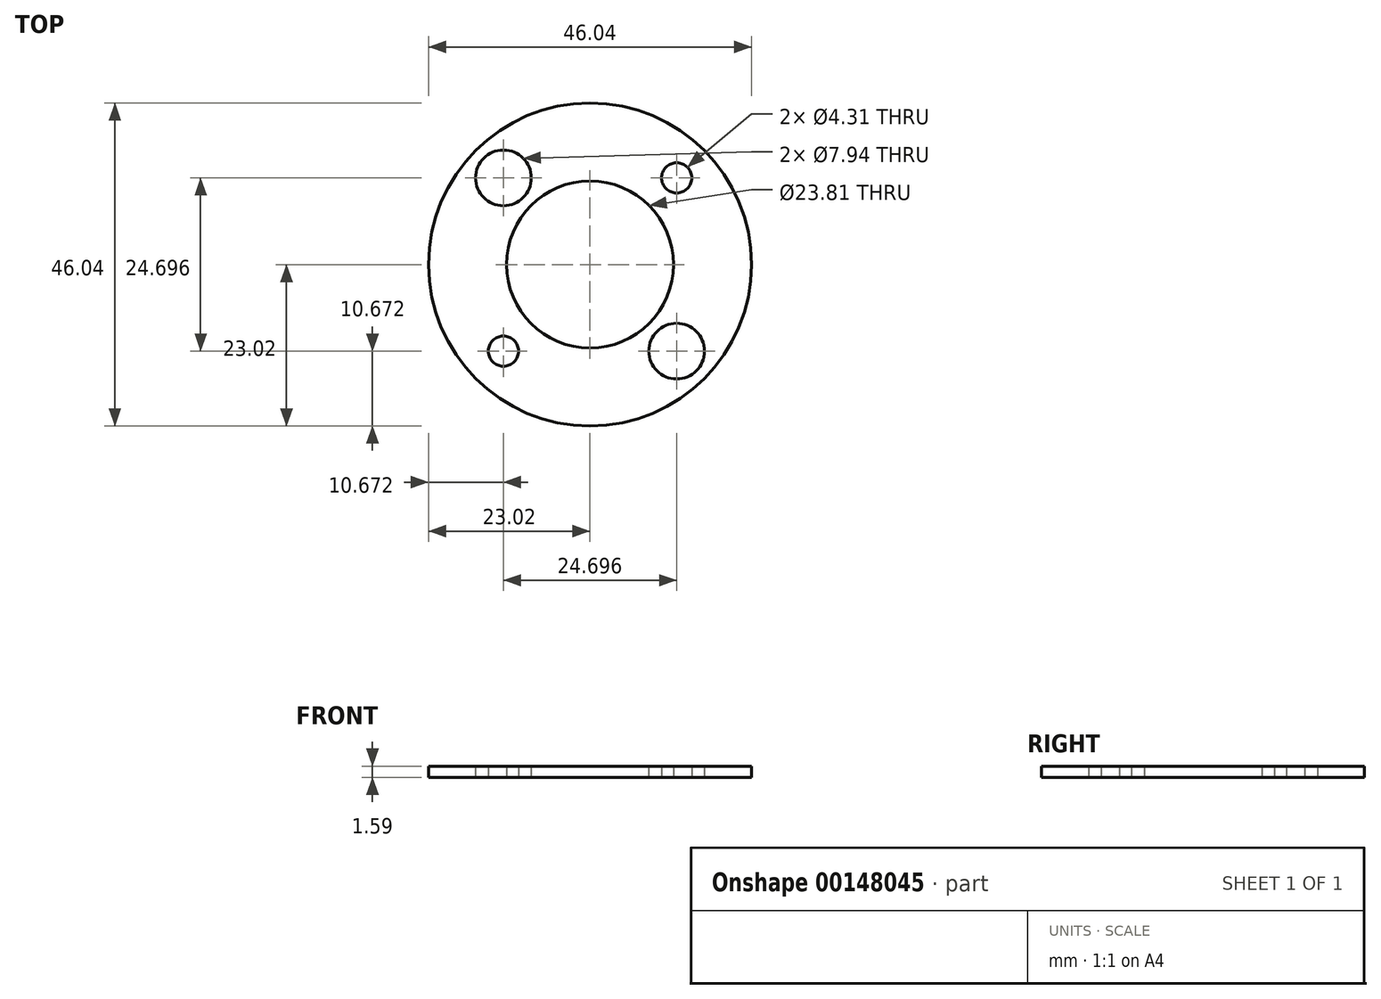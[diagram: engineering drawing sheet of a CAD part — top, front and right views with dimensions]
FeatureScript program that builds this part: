
annotation { "Feature Type Name" : "Feature", "Feature Type Description" : "" }
export const myFeature = defineFeature(function(context is Context, id is Id, definition is map)
    precondition{}
    {
        {
            var Q0;
            Q0=qCreatedBy(makeId("Top.planeOp"),FACE);
            var sketch = newSketch(context, id + "F0", { "sketchPlane" : qUnion([Q0])});
            skCircle(sketch, "E0", {"center": v(0, 0) * mm, "radius": 23.02 * mm});
            skCircle(sketch, "E1", {"center": v(0, 0) * mm, "radius": 11.9 * mm});
            skLineSegment(sketch, "E2.bottom", {"start": v(-12.35, 12.35) * mm, "end": v(12.35, 12.35) * mm, "construction": true});
            skLineSegment(sketch, "E2.top", {"start": v(-12.35, -12.35) * mm, "end": v(12.35, -12.35) * mm, "construction": true});
            skLineSegment(sketch, "E2.left", {"start": v(-12.35, 12.35) * mm, "end": v(-12.35, -12.35) * mm, "construction": true});
            skLineSegment(sketch, "E2.right", {"start": v(12.35, 12.35) * mm, "end": v(12.35, -12.35) * mm, "construction": true});
            skCircle(sketch, "E3", {"center": v(-12.35, 12.35) * mm, "radius": 5.56 * mm, "construction": true});
            skCircle(sketch, "E4", {"center": v(12.35, 12.35) * mm, "radius": 2.15 * mm});
            skCircle(sketch, "E5", {"center": v(-12.35, 12.35) * mm, "radius": 3.97 * mm});
            skCircle(sketch, "E6", {"center": v(-12.35, -12.35) * mm, "radius": 2.15 * mm});
            skCircle(sketch, "E7", {"center": v(12.35, -12.35) * mm, "radius": 3.97 * mm});
            skSolve(sketch);
        }
        {
            var Q0;
            Q0=qSketchRegion(id+"F0",true);
            extrude(context, id + "F1", {"entities" : qUnion([Q0]), "depth" : 1.59 * mm});
        }
    });
